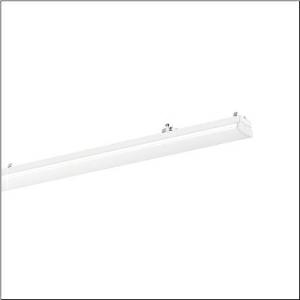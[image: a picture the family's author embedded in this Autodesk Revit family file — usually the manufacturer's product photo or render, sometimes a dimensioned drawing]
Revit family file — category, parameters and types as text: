
# Revit family: licross_r__21_recessed_opal_mo_52tl1dmn46xg_d616
name_source: partatom
category: Lighting Fixtures
units: mm (PartAtom-declared; Revit-internal decimal feet)

## family parameters
Cut with Voids When Loaded = No
Host = Face
Light Source = No
Part Type = Normal
Room Calculation Point = No
Round Connector Dimension = Use Diameter
Shared = No

## types (1)
- --- (1 x LED, 6270 lm, 35 W, 4000K)
    Apparent Load = 35 VA
    CIE Flux Codes = 44 73 91 87 100
    Color Rendering = 80
    Color Temperature = 4000K
    Default Elevation = 1800 mm
    Description = Licross® 21 recessed opal MO, luminaire insert, of sheet steel, galvanised, coil coated, white, length: 1.500mm, width: 66mm, height: 67mm, LED rated luminous flux: 6.270lm, light colour: 840, control gear: ON/OFF Multilumen, with plug, 3-pole, with phase selection, mains connection: 220..240V, AC, 50/60Hz, rated input power: 35W, internal wiring halogen-free, primary optical cover: cover, of PMMA, light emission: direct with ceiling illumination distribution, primary light characteristic: symmetric, protection rating (complete): IP40, insulation class (complete): insulation class I (protective earthing), certification: CE, ENEC, VDE, UKCA, protection symbol: D if used in an environment without relevant dust loads with corresponding accessories, impact resistance: IK06, permissible ambient temperature for indoor applications: -35..+50°C, corresponds to IFS (International Featured Standards) requirements for safety and quality in the food industry, reducing of maximum allowable ambient temperature of 5°C with ceiling mounting, LABS conformity tested according to VDMA 24364:2018-05, packaging unit: 1 piece
    Height = 83 mm
    Lamp = 1 x LED
    Lamp Light Flux = 6270 lm
    Lamp Power = 35 W
    Lamp count = 1
    Length = 1500 mm
    Luminous efficacy = 179 lm/W
    Manufacturer = Siteco
    ModVariant = No
    Model = 52TL1DMN46XG
    Mounting Place = Ceiling
    Mounting Type = Pendant
    Number of Poles = 1
    OnlyDefault = Yes
    Power Factor = 1
    Product Name = Licross® 21 recessed opal MO
    Product group = luminaire insert | ceiling pendant
    ProductGroupID = 902
    Protection Class = Protection class I
    Protection Degree = IP 40
    RLX_Detail_Level = 1
    RLX_Emergency_Light_Flux = 0 lm
    RLX_Emergency_Type = 0
    RLX_Emergency_Type_DB = No
    RlxData = <blob elided: 24553 chars, md5=7115e6eb>
    Socket = socket
    Standby Power = 0 W
    System Light Flux = 6270 lm
    System Power = 35 W
    Type Comments = factory setting: luminous flux: 100 % | (A | C | E) | 81 mA
    Type Image = l_1313666.jpg
    URL = http://relux.com
    VarID = @adj_057789
    Voltage = 0 V
    Weight = 0.00 kg
    Width = 76 mm

## geometry (parser evidence)
native form markers: Blend x4, Sweep x11
no freeform markers — native parametric forms only
